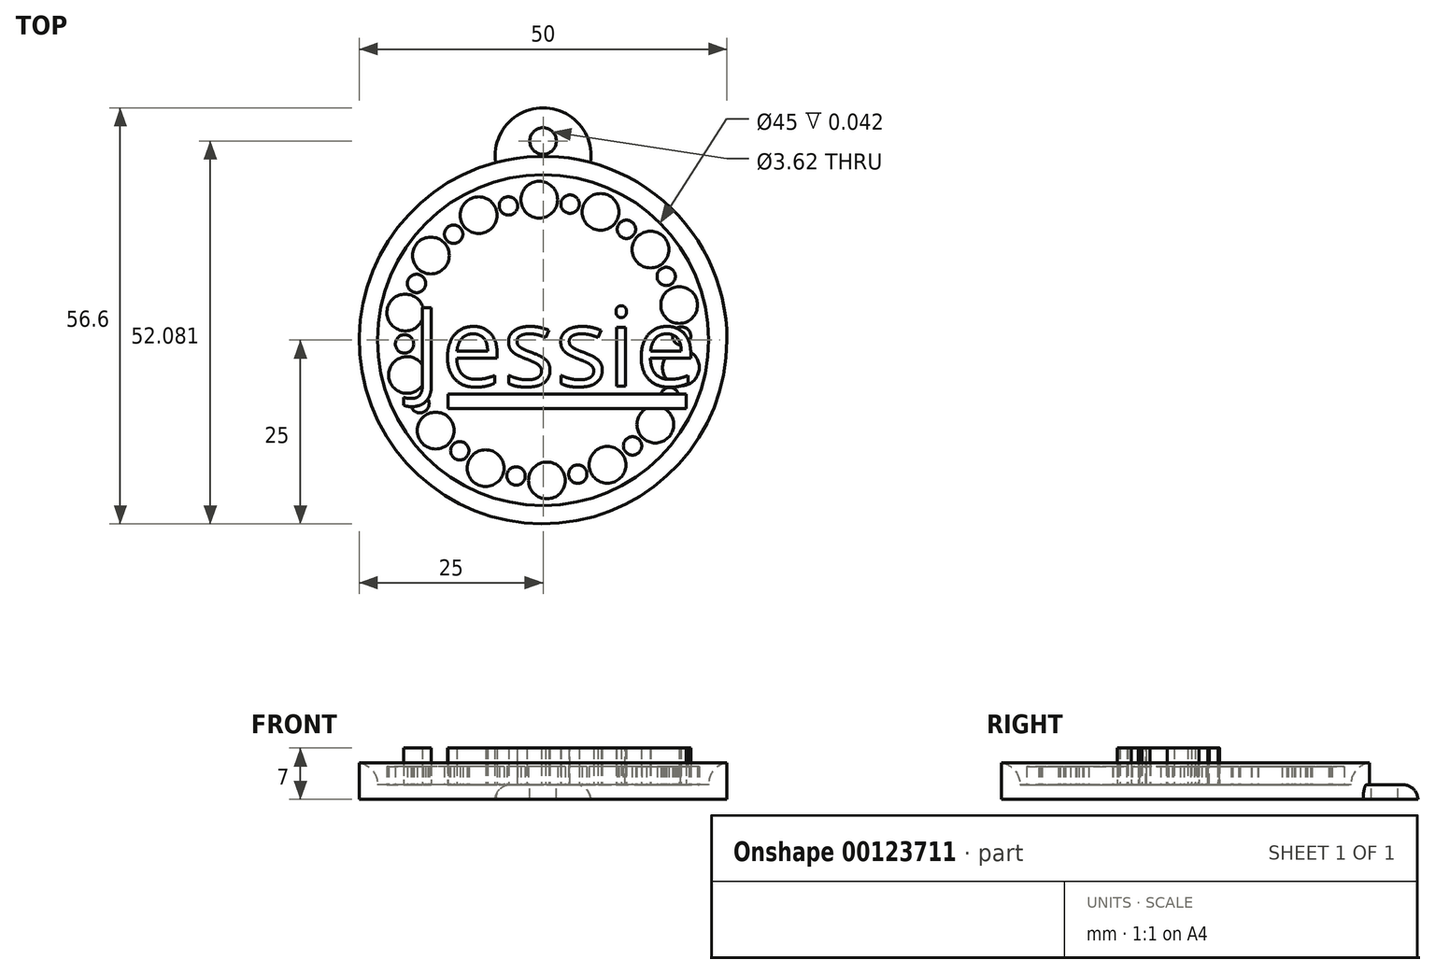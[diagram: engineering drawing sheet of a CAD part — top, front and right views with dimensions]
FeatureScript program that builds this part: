
annotation { "Feature Type Name" : "Feature", "Feature Type Description" : "" }
export const myFeature = defineFeature(function(context is Context, id is Id, definition is map)
    precondition{}
    {
        {
            var Q0;
            Q0=qCreatedBy(makeId("Top.planeOp"),FACE);
            var sketch = newSketch(context, id + "F0", { "sketchPlane" : qUnion([Q0])});
            skCircle(sketch, "E0", {"center": v(0, 0) * mm, "radius": 25 * mm});
            skCircle(sketch, "E1.0", {"center": v(0, 0) * mm, "radius": 22.5 * mm});
            skSolve(sketch);
        }
        {
            var Q0;
            Q0=makeQuery(id+"F0.imprint","IMPRINT",FACE,{"disambiguationData":[TD([[makeQuery(id+"F0.imprint","IMPRINT",EDGE,{"derivedFrom":sQuery(id+"F0.wireOp",EDGE,"E1.0")}),1.0]])]});
            extrude(context, id + "F1", {"entities" : qUnion([Q0]), "depth" : 2 * mm});
        }
        {
            var Q0;
            Q0=makeQuery(id+"F0.imprint","IMPRINT",FACE,{"disambiguationData":[TD([[makeQuery(id+"F0.imprint","IMPRINT",EDGE,{"derivedFrom":sQuery(id+"F0.wireOp",EDGE,"E0")}),1.0]])]});
            extrude(context, id + "F2", {"entities" : qUnion([Q0]), "operationType" : NewBodyOperationType.ADD, "depth" : 5 * mm});
        }
        {
            var Q0;
            Q0=makeQuery(id+"F1.opExtrude","CAP_FACE",FACE,{"disambiguationData":[OSD([sQuery(id+"F0.wireOp",EDGE,"E1.0")])],"isStart":false});
            var sketch = newSketch(context, id + "F3", { "sketchPlane" : qUnion([Q0])});
            skText(sketch, "E2", { "text": "Jessie", "fontName": "OpenSans-Regular.ttf"});
            const initialGuessF3  = {"E2": [-0.0178, -0.00626, 1, 0, 0.01072]};
            skSetInitialGuess(sketch, initialGuessF3);
            skSolve(sketch);
        }
        {
            var Q0;
            Q0 = qSketchRegion(id + "F3", true);
            extrude(context, id + "F4", {"entities" : qUnion([Q0]), "operationType" : NewBodyOperationType.ADD, "depth" : 5 * mm});
        }
        {
            var Q0;
            Q0=makeQuery(id+"F2.opExtrude","CAP_EDGE",EDGE,{"disambiguationData":[OSD([sQuery(id+"F0.wireOp",EDGE,"E1.0")])],"isStart":false});
            fillet(context, id + "F5", {"entities" : qUnion([Q0]), "radius" : 3 * mm, "tangentPropagation" : true, "allowEdgeOverflow" : false});
        }
        {
            var Q0;
            {var subQ0=sQuery(id+"F0.wireOp",EDGE,"E1.0");Q0=makeQuery(id+"F4.boolean.opBoolean","SPLIT",FACE,{"disambiguationData":[TD([makeQuery(id+"F2.opExtrude","SWEPT_FACE",FACE,{"disambiguationData":[OSD([subQ0])]})])],"derivedFrom":makeQuery(id+"F1.opExtrude","CAP_FACE",FACE,{"disambiguationData":[OSD([subQ0])],"isStart":false})});}
            var sketch = newSketch(context, id + "F6", { "sketchPlane" : qUnion([Q0])});
            skLineSegment(sketch, "E3.bottom", {"start": v(-12.9, -7.34) * mm, "end": v(19.45, -7.34) * mm});
            skLineSegment(sketch, "E3.top", {"start": v(-12.9, -9.3) * mm, "end": v(19.45, -9.3) * mm});
            skLineSegment(sketch, "E3.left", {"start": v(-12.9, -7.34) * mm, "end": v(-12.9, -9.3) * mm});
            skLineSegment(sketch, "E3.right", {"start": v(19.45, -7.34) * mm, "end": v(19.45, -9.3) * mm});
            skSolve(sketch);
        }
        {
            var Q0;
            Q0=makeQuery(id+"F6.imprint","IMPRINT",FACE,{"disambiguationData":[TD([[makeQuery(id+"F6.imprint","IMPRINT",EDGE,{"derivedFrom":sQuery(id+"F6.wireOp",EDGE,"E3.bottom")}),-1.0]])]});
            extrude(context, id + "F7", {"entities" : qUnion([Q0]), "operationType" : NewBodyOperationType.ADD, "depth" : 5 * mm});
        }
        {
            var Q0;
            {var subQ0=sQuery(id+"F0.wireOp",EDGE,"E1.0");Q0=makeQuery(id+"F4.boolean.opBoolean","SPLIT",FACE,{"disambiguationData":[TD([makeQuery(id+"F2.opExtrude","SWEPT_FACE",FACE,{"disambiguationData":[OSD([subQ0])]})])],"derivedFrom":makeQuery(id+"F1.opExtrude","CAP_FACE",FACE,{"disambiguationData":[OSD([subQ0])],"isStart":false})});}
            var sketch = newSketch(context, id + "F8", { "sketchPlane" : qUnion([Q0])});
            skCircle(sketch, "E4", {"center": v(-0.52, 19.1) * mm, "radius": 2.5 * mm});
            skCircle(sketch, "E5.1.0", {"center": v(7.82, 17.43) * mm, "radius": 2.5 * mm});
            skCircle(sketch, "E5.2.0", {"center": v(14.6, 12.31) * mm, "radius": 2.5 * mm});
            skCircle(sketch, "E5.3.0", {"center": v(18.5, 4.76) * mm, "radius": 2.5 * mm});
            skCircle(sketch, "E5.4.0", {"center": v(18.73, -3.74) * mm, "radius": 2.5 * mm});
            skCircle(sketch, "E5.5.0", {"center": v(15.25, -11.5) * mm, "radius": 2.5 * mm});
            skCircle(sketch, "E5.6.0", {"center": v(8.76, -16.98) * mm, "radius": 2.5 * mm});
            skCircle(sketch, "E5.7.0", {"center": v(0.52, -19.1) * mm, "radius": 2.5 * mm});
            skCircle(sketch, "E5.8.0", {"center": v(-7.82, -17.43) * mm, "radius": 2.5 * mm});
            skCircle(sketch, "E5.9.0", {"center": v(-14.6, -12.31) * mm, "radius": 2.5 * mm});
            skCircle(sketch, "E5.10.0", {"center": v(-18.5, -4.76) * mm, "radius": 2.5 * mm});
            skCircle(sketch, "E5.11.0", {"center": v(-18.73, 3.74) * mm, "radius": 2.5 * mm});
            skCircle(sketch, "E5.12.0", {"center": v(-15.25, 11.5) * mm, "radius": 2.5 * mm});
            skCircle(sketch, "E5.13.0", {"center": v(-8.76, 16.98) * mm, "radius": 2.5 * mm});
            skPoint(sketch, "E5.center", {"position": v(0, 0) * mm});
            skLineSegment(sketch, "E5.anchor1", {"start": v(0, 0) * mm, "end": v(-0.52, 19.1) * mm, "construction": true});
            skLineSegment(sketch, "E5.anchor2", {"start": v(0, 0) * mm, "end": v(-8.76, 16.98) * mm, "construction": true});
            skSolve(sketch);
        }
        {
            var Q0;
            Q0=makeQuery(id+"F8.imprint","IMPRINT",FACE,{"disambiguationData":[TD([[makeQuery(id+"F8.imprint","IMPRINT",EDGE,{"derivedFrom":sQuery(id+"F8.wireOp",EDGE,"E5.13.0")}),1.0]])]});
            var Q1;
            Q1=makeQuery(id+"F8.imprint","IMPRINT",FACE,{"disambiguationData":[TD([[makeQuery(id+"F8.imprint","IMPRINT",EDGE,{"derivedFrom":sQuery(id+"F8.wireOp",EDGE,"E4")}),1.0]])]});
            var Q2;
            Q2=makeQuery(id+"F8.imprint","IMPRINT",FACE,{"disambiguationData":[TD([[makeQuery(id+"F8.imprint","IMPRINT",EDGE,{"derivedFrom":sQuery(id+"F8.wireOp",EDGE,"E5.1.0")}),1.0]])]});
            var Q3;
            Q3=makeQuery(id+"F8.imprint","IMPRINT",FACE,{"disambiguationData":[TD([[makeQuery(id+"F8.imprint","IMPRINT",EDGE,{"derivedFrom":sQuery(id+"F8.wireOp",EDGE,"E5.2.0")}),1.0]])]});
            var Q4;
            Q4=makeQuery(id+"F8.imprint","IMPRINT",FACE,{"disambiguationData":[TD([[makeQuery(id+"F8.imprint","IMPRINT",EDGE,{"derivedFrom":sQuery(id+"F8.wireOp",EDGE,"E5.3.0")}),1.0]])]});
            var Q5;
            {var subQ2=makeQuery(id+"F4.opExtrude","CAP_EDGE",EDGE,{"disambiguationData":[OSD([sQuery(id+"F3.wireOp",EDGE,"E2.sketch_text.stroke-97")])],"isStart":true});Q5=makeQuery(id+"F8.imprint","IMPRINT",FACE,{"disambiguationData":[TD([[makeQuery(id+"F8.imprint","IMPRINT",EDGE,{"derivedFrom":subQ2}),1.0]])]});}
            var Q6;
            {var subQ0=sQuery(id+"F8.wireOp",EDGE,"E5.5.0");var subQ1=makeQuery(id+"F7.opExtrude","CAP_EDGE",EDGE,{"disambiguationData":[OSD([sQuery(id+"F6.wireOp",EDGE,"E3.top")])],"isStart":true});var subQ2=makeQuery(id+"F8.imprint","INTERSECT",VERTEX,{"disambiguationData":[OD(0.0)],"derivedFrom":[subQ1,subQ0]});Q6=makeQuery(id+"F8.imprint","IMPRINT",FACE,{"disambiguationData":[TD([[makeQuery(id+"F8.imprint","IMPRINT",EDGE,{"disambiguationData":[TD([[subQ2,-1.0]])],"derivedFrom":subQ0}),1.0]])]});}
            var Q7;
            Q7=makeQuery(id+"F8.imprint","IMPRINT",FACE,{"disambiguationData":[TD([[makeQuery(id+"F8.imprint","IMPRINT",EDGE,{"derivedFrom":sQuery(id+"F8.wireOp",EDGE,"E5.6.0")}),1.0]])]});
            var Q8;
            Q8=makeQuery(id+"F8.imprint","IMPRINT",FACE,{"disambiguationData":[TD([[makeQuery(id+"F8.imprint","IMPRINT",EDGE,{"derivedFrom":sQuery(id+"F8.wireOp",EDGE,"E5.7.0")}),1.0]])]});
            var Q9;
            Q9=makeQuery(id+"F8.imprint","IMPRINT",FACE,{"disambiguationData":[TD([[makeQuery(id+"F8.imprint","IMPRINT",EDGE,{"derivedFrom":sQuery(id+"F8.wireOp",EDGE,"E5.8.0")}),1.0]])]});
            var Q10;
            Q10=makeQuery(id+"F8.imprint","IMPRINT",FACE,{"disambiguationData":[TD([[makeQuery(id+"F8.imprint","IMPRINT",EDGE,{"derivedFrom":sQuery(id+"F8.wireOp",EDGE,"E5.9.0")}),1.0]])]});
            var Q11;
            {var subQ0=sQuery(id+"F8.wireOp",EDGE,"E5.10.0");var subQ1=makeQuery(id+"F4.opExtrude","CAP_EDGE",EDGE,{"disambiguationData":[OSD([sQuery(id+"F3.wireOp",EDGE,"E2.sketch_text.stroke-4")])],"isStart":true});var subQ2=makeQuery(id+"F8.imprint","INTERSECT",VERTEX,{"derivedFrom":[subQ1,subQ0]});Q11=makeQuery(id+"F8.imprint","IMPRINT",FACE,{"disambiguationData":[TD([[makeQuery(id+"F8.imprint","IMPRINT",EDGE,{"disambiguationData":[TD([[subQ2,1.0]])],"derivedFrom":subQ0}),1.0]])]});}
            var Q12;
            {var subQ0=sQuery(id+"F8.wireOp",EDGE,"E5.11.0");var subQ1=makeQuery(id+"F4.opExtrude","CAP_EDGE",EDGE,{"disambiguationData":[OSD([sQuery(id+"F3.wireOp",EDGE,"E2.sketch_text.stroke-5")])],"isStart":true});var subQ2=makeQuery(id+"F8.imprint","INTERSECT",VERTEX,{"derivedFrom":[subQ1,subQ0]});Q12=makeQuery(id+"F8.imprint","IMPRINT",FACE,{"disambiguationData":[TD([[makeQuery(id+"F8.imprint","IMPRINT",EDGE,{"disambiguationData":[TD([[subQ2,1.0]])],"derivedFrom":subQ0}),1.0]])]});}
            var Q13;
            Q13=makeQuery(id+"F8.imprint","IMPRINT",FACE,{"disambiguationData":[TD([[makeQuery(id+"F8.imprint","IMPRINT",EDGE,{"derivedFrom":sQuery(id+"F8.wireOp",EDGE,"E5.12.0")}),1.0]])]});
            extrude(context, id + "F9", {"entities" : qUnion([Q0, Q1, Q2, Q3, Q4, Q5, Q6, Q7, Q8, Q9, Q10, Q11, Q12, Q13]), "operationType" : NewBodyOperationType.ADD, "depth" : 2.5 * mm});
        }
        {
            var Q0;
            {var subQ69=sQuery(id+"F0.wireOp",EDGE,"E1.0");var subQ70=makeQuery(id+"F2.opExtrude","SWEPT_FACE",FACE,{"disambiguationData":[OSD([subQ69])]});Q0=makeQuery(id+"F9.boolean.opBoolean","SPLIT",FACE,{"disambiguationData":[TD([subQ70])],"derivedFrom":makeQuery(id+"F4.boolean.opBoolean","SPLIT",FACE,{"disambiguationData":[TD([subQ70])],"derivedFrom":makeQuery(id+"F1.opExtrude","CAP_FACE",FACE,{"disambiguationData":[OSD([subQ69])],"isStart":false})})});}
            var sketch = newSketch(context, id + "F10", { "sketchPlane" : qUnion([Q0])});
            skCircle(sketch, "E6", {"center": v(-12.17, 14.4) * mm, "radius": 1.25 * mm});
            skCircle(sketch, "E7.1.0", {"center": v(-17.2, 7.7) * mm, "radius": 1.25 * mm});
            skCircle(sketch, "E7.2.0", {"center": v(-18.84, -0.54) * mm, "radius": 1.25 * mm});
            skCircle(sketch, "E7.3.0", {"center": v(-16.74, -8.66) * mm, "radius": 1.25 * mm});
            skCircle(sketch, "E7.4.0", {"center": v(-11.33, -15.06) * mm, "radius": 1.25 * mm});
            skCircle(sketch, "E7.5.0", {"center": v(-3.67, -18.49) * mm, "radius": 1.25 * mm});
            skCircle(sketch, "E7.6.0", {"center": v(4.72, -18.25) * mm, "radius": 1.25 * mm});
            skCircle(sketch, "E7.7.0", {"center": v(12.17, -14.4) * mm, "radius": 1.25 * mm});
            skCircle(sketch, "E7.8.0", {"center": v(17.2, -7.7) * mm, "radius": 1.25 * mm});
            skCircle(sketch, "E7.9.0", {"center": v(18.84, 0.54) * mm, "radius": 1.25 * mm});
            skCircle(sketch, "E7.10.0", {"center": v(16.74, 8.66) * mm, "radius": 1.25 * mm});
            skCircle(sketch, "E7.11.0", {"center": v(11.33, 15.06) * mm, "radius": 1.25 * mm});
            skCircle(sketch, "E7.12.0", {"center": v(3.67, 18.49) * mm, "radius": 1.25 * mm});
            skCircle(sketch, "E7.13.0", {"center": v(-4.72, 18.25) * mm, "radius": 1.25 * mm});
            skPoint(sketch, "E7.center", {"position": v(0, 0) * mm});
            skSolve(sketch);
        }
        {
            var Q0;
            Q0=makeQuery(id+"F10.imprint","IMPRINT",FACE,{"disambiguationData":[TD([[makeQuery(id+"F10.imprint","IMPRINT",EDGE,{"derivedFrom":sQuery(id+"F10.wireOp",EDGE,"E6")}),1.0]])]});
            var Q1;
            Q1=makeQuery(id+"F10.imprint","IMPRINT",FACE,{"disambiguationData":[TD([[makeQuery(id+"F10.imprint","IMPRINT",EDGE,{"derivedFrom":sQuery(id+"F10.wireOp",EDGE,"E7.13.0")}),1.0]])]});
            var Q2;
            Q2=makeQuery(id+"F10.imprint","IMPRINT",FACE,{"disambiguationData":[TD([[makeQuery(id+"F10.imprint","IMPRINT",EDGE,{"derivedFrom":sQuery(id+"F10.wireOp",EDGE,"E7.12.0")}),1.0]])]});
            var Q3;
            Q3=makeQuery(id+"F10.imprint","IMPRINT",FACE,{"disambiguationData":[TD([[makeQuery(id+"F10.imprint","IMPRINT",EDGE,{"derivedFrom":sQuery(id+"F10.wireOp",EDGE,"E7.11.0")}),1.0]])]});
            var Q4;
            Q4=makeQuery(id+"F10.imprint","IMPRINT",FACE,{"disambiguationData":[TD([[makeQuery(id+"F10.imprint","IMPRINT",EDGE,{"derivedFrom":sQuery(id+"F10.wireOp",EDGE,"E7.10.0")}),1.0]])]});
            var Q5;
            {var subQ0=sQuery(id+"F10.wireOp",EDGE,"E7.9.0");var subQ1=makeQuery(id+"F4.opExtrude","CAP_EDGE",EDGE,{"disambiguationData":[OSD([sQuery(id+"F3.wireOp",EDGE,"E2.sketch_text.stroke-95")])],"isStart":true});var subQ2=makeQuery(id+"F10.imprint","INTERSECT",VERTEX,{"derivedFrom":[subQ1,subQ0]});Q5=makeQuery(id+"F10.imprint","IMPRINT",FACE,{"disambiguationData":[TD([[makeQuery(id+"F10.imprint","IMPRINT",EDGE,{"disambiguationData":[TD([[subQ2,1.0]])],"derivedFrom":subQ0}),1.0]])]});}
            var Q6;
            {var subQ0=sQuery(id+"F10.wireOp",EDGE,"E7.9.0");var subQ1=makeQuery(id+"F4.opExtrude","CAP_EDGE",EDGE,{"disambiguationData":[OSD([sQuery(id+"F3.wireOp",EDGE,"E2.sketch_text.stroke-95")])],"isStart":true});var subQ2=makeQuery(id+"F10.imprint","INTERSECT",VERTEX,{"derivedFrom":[subQ1,subQ0]});Q6=makeQuery(id+"F10.imprint","IMPRINT",FACE,{"disambiguationData":[TD([[makeQuery(id+"F10.imprint","IMPRINT",EDGE,{"disambiguationData":[TD([[subQ2,-1.0]])],"derivedFrom":subQ0}),1.0]])]});}
            var Q7;
            {var subQ0=sQuery(id+"F10.wireOp",EDGE,"E7.8.0");var subQ1=makeQuery(id+"F7.opExtrude","CAP_EDGE",EDGE,{"disambiguationData":[OSD([sQuery(id+"F6.wireOp",EDGE,"E3.bottom")])],"isStart":true});var subQ2=makeQuery(id+"F10.imprint","INTERSECT",VERTEX,{"disambiguationData":[OD(0.0)],"derivedFrom":[subQ1,subQ0]});Q7=makeQuery(id+"F10.imprint","IMPRINT",FACE,{"disambiguationData":[TD([[makeQuery(id+"F10.imprint","IMPRINT",EDGE,{"disambiguationData":[TD([[subQ2,1.0]])],"derivedFrom":subQ0}),1.0]])]});}
            var Q8;
            Q8=makeQuery(id+"F10.imprint","IMPRINT",FACE,{"disambiguationData":[TD([[makeQuery(id+"F10.imprint","IMPRINT",EDGE,{"derivedFrom":sQuery(id+"F10.wireOp",EDGE,"E7.7.0")}),1.0]])]});
            var Q9;
            Q9=makeQuery(id+"F10.imprint","IMPRINT",FACE,{"disambiguationData":[TD([[makeQuery(id+"F10.imprint","IMPRINT",EDGE,{"derivedFrom":sQuery(id+"F10.wireOp",EDGE,"E7.6.0")}),1.0]])]});
            var Q10;
            Q10=makeQuery(id+"F10.imprint","IMPRINT",FACE,{"disambiguationData":[TD([[makeQuery(id+"F10.imprint","IMPRINT",EDGE,{"derivedFrom":sQuery(id+"F10.wireOp",EDGE,"E7.5.0")}),1.0]])]});
            var Q11;
            Q11=makeQuery(id+"F10.imprint","IMPRINT",FACE,{"disambiguationData":[TD([[makeQuery(id+"F10.imprint","IMPRINT",EDGE,{"derivedFrom":sQuery(id+"F10.wireOp",EDGE,"E7.4.0")}),1.0]])]});
            var Q12;
            {var subQ0=sQuery(id+"F10.wireOp",EDGE,"E7.3.0");var subQ1=makeQuery(id+"F4.opExtrude","CAP_EDGE",EDGE,{"disambiguationData":[OSD([sQuery(id+"F3.wireOp",EDGE,"E2.sketch_text.stroke-8")])],"isStart":true});var subQ2=makeQuery(id+"F10.imprint","INTERSECT",VERTEX,{"derivedFrom":[subQ1,subQ0]});Q12=makeQuery(id+"F10.imprint","IMPRINT",FACE,{"disambiguationData":[TD([[makeQuery(id+"F10.imprint","IMPRINT",EDGE,{"disambiguationData":[TD([[subQ2,1.0]])],"derivedFrom":subQ0}),1.0]])]});}
            var Q13;
            Q13=makeQuery(id+"F10.imprint","IMPRINT",FACE,{"disambiguationData":[TD([[makeQuery(id+"F10.imprint","IMPRINT",EDGE,{"derivedFrom":sQuery(id+"F10.wireOp",EDGE,"E7.2.0")}),1.0]])]});
            var Q14;
            Q14=makeQuery(id+"F10.imprint","IMPRINT",FACE,{"disambiguationData":[TD([[makeQuery(id+"F10.imprint","IMPRINT",EDGE,{"derivedFrom":sQuery(id+"F10.wireOp",EDGE,"E7.1.0")}),1.0]])]});
            extrude(context, id + "F11", {"entities" : qUnion([Q0, Q1, Q2, Q3, Q4, Q5, Q6, Q7, Q8, Q9, Q10, Q11, Q12, Q13, Q14]), "operationType" : NewBodyOperationType.ADD, "depth" : 2.5 * mm});
        }
        {
            var Q0;
            Q0=makeQuery(id+"F0.imprint","IMPRINT",FACE,{"disambiguationData":[TD([[makeQuery(id+"F0.imprint","IMPRINT",EDGE,{"derivedFrom":sQuery(id+"F0.wireOp",EDGE,"E0")}),1.0]])]});
            var sketch = newSketch(context, id + "F12", { "sketchPlane" : qUnion([Q0])});
            skCircle(sketch, "E8", {"center": v(0, 25.1) * mm, "radius": 6.5 * mm});
            skSolve(sketch);
        }
        {
            var Q0;
            {var subQ0=sQuery(id+"F12.wireOp",EDGE,"E8");var subQ1=makeQuery(id+"F0.imprint","IMPRINT",EDGE,{"derivedFrom":sQuery(id+"F0.wireOp",EDGE,"E0")});var subQ2=makeQuery(id+"F12.imprint","INTERSECT",VERTEX,{"disambiguationData":[OD(0.0)],"derivedFrom":[subQ1,subQ0]});Q0=makeQuery(id+"F12.imprint","IMPRINT",FACE,{"disambiguationData":[TD([[makeQuery(id+"F12.imprint","IMPRINT",EDGE,{"disambiguationData":[TD([[subQ2,1.0]])],"derivedFrom":subQ0}),1.0]])]});}
            extrude(context, id + "F13", {"entities" : qUnion([Q0]), "operationType" : NewBodyOperationType.ADD, "depth" : 2 * mm});
        }
        {
            var Q0;
            Q0=makeQuery(id+"F13.opExtrude","CAP_EDGE",EDGE,{"disambiguationData":[OSD([sQuery(id+"F12.wireOp",EDGE,"E8")])],"isStart":false});
            fillet(context, id + "F14", {"entities" : qUnion([Q0]), "radius" : 2 * mm, "tangentPropagation" : true, "allowEdgeOverflow" : false});
        }
        {
            var Q0;
            Q0=makeQuery(id+"F13.opExtrude","CAP_FACE",FACE,{"disambiguationData":[OSD([sQuery(id+"F0.wireOp",EDGE,"E0"),sQuery(id+"F12.wireOp",EDGE,"E8")])],"isStart":false});
            var sketch = newSketch(context, id + "F15", { "sketchPlane" : qUnion([Q0])});
            skCircle(sketch, "E9", {"center": v(0, 27.08) * mm, "radius": 1.8 * mm});
            skSolve(sketch);
        }
        {
            var Q0;
            Q0=makeQuery(id+"F15.imprint","IMPRINT",FACE,{"disambiguationData":[TD([[makeQuery(id+"F15.imprint","IMPRINT",EDGE,{"derivedFrom":sQuery(id+"F15.wireOp",EDGE,"E9")}),1.0]])]});
            extrude(context, id + "F16", {"entities" : qUnion([Q0]), "operationType" : NewBodyOperationType.REMOVE, "oppositeDirection" : true, "depth" : 2 * mm});
        }
    });
